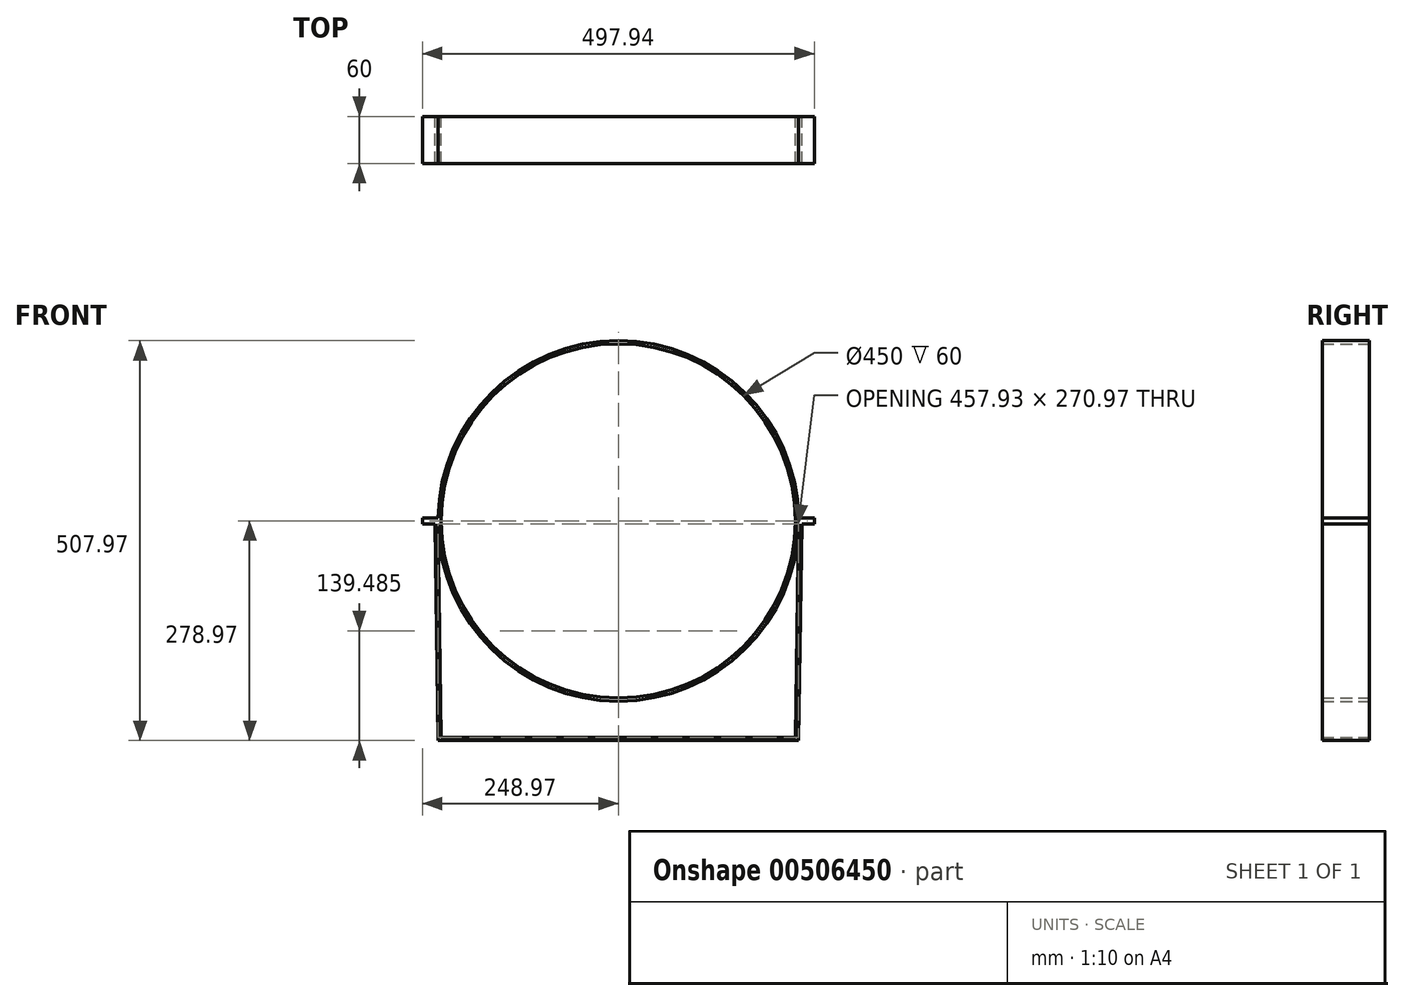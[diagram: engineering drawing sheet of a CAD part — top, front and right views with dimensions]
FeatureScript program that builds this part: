
annotation { "Feature Type Name" : "Feature", "Feature Type Description" : "" }
export const myFeature = defineFeature(function(context is Context, id is Id, definition is map)
    precondition{}
    {
        {
            var Q0;
            Q0=qCreatedBy(makeId("Front.planeOp"),FACE);
            var sketch = newSketch(context, id + "F0", { "sketchPlane" : qUnion([Q0])});
            skCircle(sketch, "E0", {"center": v(0, 0) * mm, "radius": 225 * mm});
            skCircle(sketch, "E1", {"center": v(0, 0) * mm, "radius": 229 * mm});
            skLineSegment(sketch, "E2", {"start": v(0, 0) * mm, "end": v(-690.21, 0) * mm, "construction": true});
            skLineSegment(sketch, "E3", {"start": v(-228.97, 4) * mm, "end": v(-248.97, 4) * mm});
            skLineSegment(sketch, "E4", {"start": v(-248.97, 4) * mm, "end": v(-248.97, 0) * mm});
            skLineSegment(sketch, "E5.MirrorCS", {"start": v(-228.97, -4) * mm, "end": v(-248.97, -4) * mm});
            skLineSegment(sketch, "E6.MirrorCS", {"start": v(-248.97, -4) * mm, "end": v(-248.97, 0) * mm});
            skLineSegment(sketch, "E7", {"start": v(0, 0) * mm, "end": v(0, 668.71) * mm, "construction": true});
            skLineSegment(sketch, "E8.MirrorCS", {"start": v(248.97, 4) * mm, "end": v(248.97, 0) * mm});
            skLineSegment(sketch, "E9.MirrorCS", {"start": v(248.97, -4) * mm, "end": v(248.97, 0) * mm});
            skLineSegment(sketch, "E10.MirrorCS", {"start": v(228.97, 4) * mm, "end": v(248.97, 4) * mm});
            skLineSegment(sketch, "E11.MirrorCS", {"start": v(228.97, -4) * mm, "end": v(248.97, -4) * mm});
            skLineSegment(sketch, "E12", {"start": v(-228.97, -4) * mm, "end": v(-232.97, -4) * mm});
            skLineSegment(sketch, "E13", {"start": v(-232.97, -4) * mm, "end": v(-228.97, -278.97) * mm});
            skLineSegment(sketch, "E14", {"start": v(-228.97, -4) * mm, "end": v(-225.02, -274.97) * mm});
            skLineSegment(sketch, "E15.MirrorCS", {"start": v(228.97, -4) * mm, "end": v(225.02, -274.97) * mm});
            skLineSegment(sketch, "E16.MirrorCS", {"start": v(232.97, -4) * mm, "end": v(228.97, -278.97) * mm});
            skLineSegment(sketch, "E17", {"start": v(-228.97, -278.97) * mm, "end": v(228.97, -278.97) * mm});
            skLineSegment(sketch, "E18", {"start": v(-225.02, -274.97) * mm, "end": v(225.02, -274.97) * mm});
            skSolve(sketch);
        }
        {
            var Q0;
            Q0=qSketchRegion(id+"F0",true);
            extrude(context, id + "F1", {"entities" : qUnion([Q0]), "offsetDistance" : 25 * mm, "depth" : 60 * mm});
        }
    });
